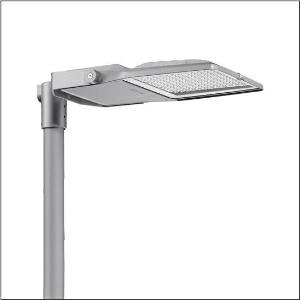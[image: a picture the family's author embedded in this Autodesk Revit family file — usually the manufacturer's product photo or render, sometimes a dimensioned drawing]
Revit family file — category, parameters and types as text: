
# Revit family: floodlight_fl_21_iq_midi___pl43_5xa7782e2a3a_72be
name_source: partatom
category: Lighting Fixtures
units: mm (PartAtom-declared; Revit-internal decimal feet)

## family parameters
Cut with Voids When Loaded = No
Host = Face
Light Source = No
Part Type = Normal
Room Calculation Point = No
Round Connector Dimension = Use Diameter
Shared = No

## types (1)
- --- (1 x LED, 27540 lm, 208.1 W, 3000K)
    Apparent Load = 208 VA
    CIE Flux Codes = 27 78 99 100 100
    Color Rendering = 70
    Color Temperature = 3000K
    Default Elevation = 1800 mm
    Description = Floodlight FL 21 iQ midi, floodlight, primary light control with lens, of PMMA, primary optical cover: protective disc, of toughened safety glass, transparent, light distribution: PL43, light emission: direct distribution, installation type: surface-mounted, LED, High Power LED, rated luminous flux: 27.540lm, luminous efficacy: 132lm/W, light colour: 730, colour temperature: 3000K, control gear: ECG iQ, control: optimised constant luminous flux control (CLO 2.0), Desk-Remote (wireless, voltage-free reading and setting of iQ features in the workshop via application-optimized NFC function/RFID function), Smart-Wire, Night-Set, Temp-Guard, Auto-Match, Street-Remote, with terminal, 6-pole, mains connection: 220..240V, AC, 50/60Hz, start of lifetime: 208W, end of service life: 227W, reduction: 90W, luminaire housing, of diecast aluminium, powder-coated, Siteco® metallic grey (DB 702S), corrosivity category C5 mid according to DIN EN ISO 12944, sealing non-destructively replaceable, please order mast flange separately, mast bracket, of steel, galvanised, powder-coated, Siteco® metallic grey (DB 702S), protection rating (complete): IP66, insulation class (complete): insulation class II (safety insulation), certification: CE, protection symbol: D, impact resistance: IK08, permissible operating ambient temperature: -40..+40°C, permissible operating ambient temperature for outdoor applications: -40..+50°C, standard: DIN EN 12944, LABS conformity tested according to VDMA 24364:2018-05, packaging unit: 1 piece

Light Distribution: PL43
    Height = 76 mm
    Lamp = 1 x LED
    Lamp Light Flux = 27540 lm
    Lamp Power = 208.1 W
    Lamp count = 1
    Length = 657 mm
    Luminous efficacy = 132 lm/W
    Manufacturer = Siteco
    ModVariant = No
    Model = 5XA7782E2A3A
    Number of Poles = 1
    OnlyDefault = Yes
    Power Factor = 1
    Product Name = Floodlight FL 21 iQ midi | PL43
    Product group = floodlight | pylon annexe
    ProductGroupID = 6200
    Protection Class = Protection class II
    Protection Degree = IP 66
    RLX_Detail_Level = 1
    RLX_Emergency_Light_Flux = 0 lm
    RLX_Emergency_Type = 0
    RLX_Emergency_Type_DB = No
    RlxData = <blob elided: 153317 chars, md5=941fdbe7>
    Socket = socket
    Standby Power = 0 W
    System Light Flux = 27540 lm
    System Power = 208 W
    Type Comments = factory setting: luminous flux: 100 % | dim-lin: 254 | 710 mA
    Type Image = l_1007123.jpg
    URL = http://relux.com
    VarID = @adj_035313
    Voltage = 0 V
    Weight = 0.00 kg
    Width = 442 mm

## geometry (parser evidence)
native form markers: Blend x4, Sweep x12
no freeform markers — native parametric forms only
